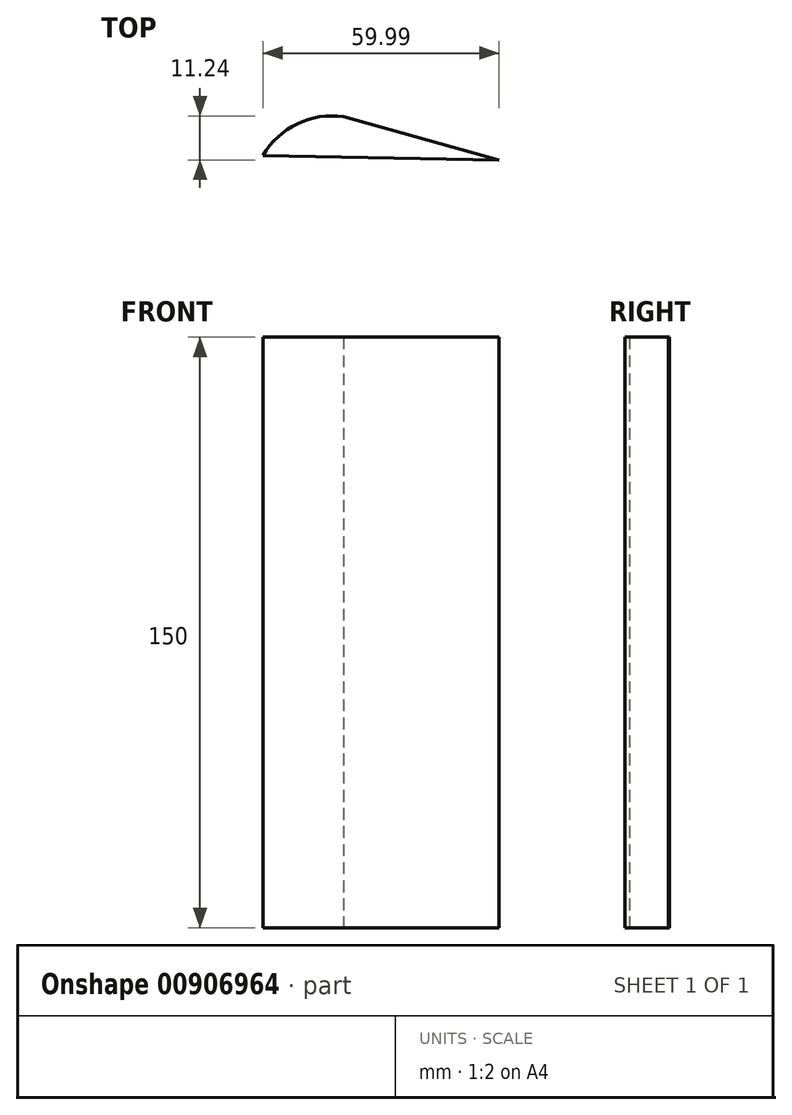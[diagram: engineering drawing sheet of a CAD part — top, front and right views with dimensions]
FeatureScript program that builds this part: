
annotation { "Feature Type Name" : "Feature", "Feature Type Description" : "" }
export const myFeature = defineFeature(function(context is Context, id is Id, definition is map)
    precondition{}
    {
        {
            var Q0;
            Q0=qCreatedBy(makeId("Top.planeOp"),FACE);
            var sketch = newSketch(context, id + "F0", { "sketchPlane" : qUnion([Q0])});
            skLineSegment(sketch, "E0", {"start": v(0, 0) * mm, "end": v(-59.99, 1.13) * mm});
            skArc(sketch, "E1", {"start": v(-39.58, 11.04) * mm, "mid": v(-51.3, 9.21) * mm, "end": v(-59.99, 1.13) * mm});
            skLineSegment(sketch, "E2", {"start": v(-39.58, 11.04) * mm, "end": v(0, 0) * mm});
            skSolve(sketch);
        }
        {
            var Q0;
            Q0 = qSketchRegion(id + "F0", true);
            extrude(context, id + "F1", {"entities" : qUnion([Q0]), "depth" : 150 * mm, "offsetDistance" : 25 * mm});
        }
    });
